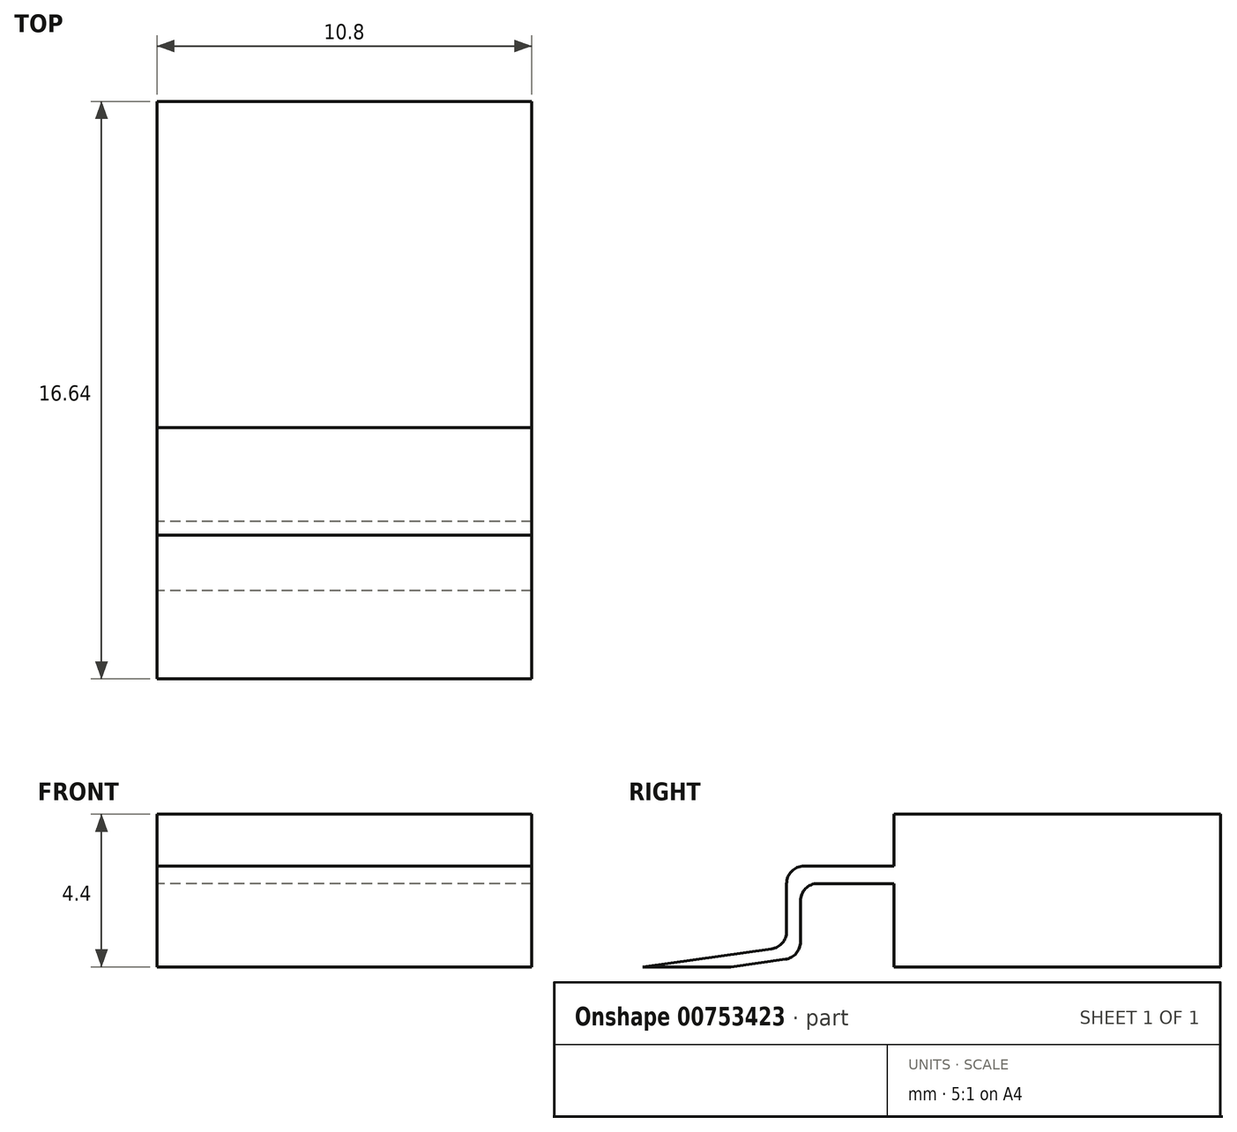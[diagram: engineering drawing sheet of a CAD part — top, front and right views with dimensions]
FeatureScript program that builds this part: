
annotation { "Feature Type Name" : "Feature", "Feature Type Description" : "" }
export const myFeature = defineFeature(function(context is Context, id is Id, definition is map)
    precondition{}
    {
        {
            var Q0;
            Q0=qCreatedBy(makeId("Top.planeOp"),FACE);
            var sketch = newSketch(context, id + "F0", { "sketchPlane" : qUnion([Q0])});
            skLineSegment(sketch, "E0.bottom", {"start": v(-5.4, -4.7) * mm, "end": v(5.4, -4.7) * mm});
            skLineSegment(sketch, "E0.top", {"start": v(-5.4, 4.7) * mm, "end": v(5.4, 4.7) * mm});
            skLineSegment(sketch, "E0.left", {"start": v(-5.4, 4.7) * mm, "end": v(-5.4, -4.7) * mm});
            skLineSegment(sketch, "E0.right", {"start": v(5.4, 4.7) * mm, "end": v(5.4, -4.7) * mm});
            skSolve(sketch);
        }
        {
            var Q0;
            Q0 = qSketchRegion(id + "F0", true);
            extrude(context, id + "F1", {"entities" : qUnion([Q0]), "depth" : 4.4 * mm, "offsetDistance" : 25 * mm});
        }
        {
            var Q0;
            Q0=makeQuery(id+"F1.opExtrude","SWEPT_FACE",FACE,{"disambiguationData":[OSD([sQuery(id+"F0.wireOp",EDGE,"E0.left")])]});
            var sketch = newSketch(context, id + "F2", { "sketchPlane" : qUnion([Q0])});
            skLineSegment(sketch, "E1.bottom", {"start": v(4.7, 2.9) * mm, "end": v(7.8, 2.9) * mm});
            skLineSegment(sketch, "E1.top", {"start": v(4.7, 2.4) * mm, "end": v(7.8, 2.4) * mm});
            skLineSegment(sketch, "E1.left", {"start": v(4.7, 2.9) * mm, "end": v(4.7, 2.4) * mm});
            skLineSegment(sketch, "E1.right", {"start": v(7.8, 2.9) * mm, "end": v(7.8, 2.4) * mm});
            skLineSegment(sketch, "E2.left", {"start": v(7.8, 2.9) * mm, "end": v(7.8, 0.58) * mm});
            skLineSegment(sketch, "E3", {"start": v(7.4, 0.28) * mm, "end": v(9.4, 0) * mm});
            skLineSegment(sketch, "E4", {"start": v(7.4, 0.28) * mm, "end": v(7.8, 0.58) * mm});
            skLineSegment(sketch, "E5", {"start": v(7.8, 0.58) * mm, "end": v(11.94, 0) * mm});
            skLineSegment(sketch, "E6", {"start": v(9.4, 0) * mm, "end": v(9.8, 0.3) * mm});
            skLineSegment(sketch, "E7", {"start": v(7.4, 0.28) * mm, "end": v(7.4, 2.4) * mm});
            skLineSegment(sketch, "E8", {"start": v(9.4, 0) * mm, "end": v(11.94, 0) * mm});
            skSolve(sketch);
        }
        {
            var Q0;
            {var subQ5=sQuery(id+"F2.wireOp",EDGE,"E1.bottom");Q0=makeQuery(id+"F2.imprint","IMPRINT",FACE,{"disambiguationData":[TD([[makeQuery(id+"F2.imprint","IMPRINT",EDGE,{"derivedFrom":subQ5}),-1.0]])]});}
            var Q1;
            {var subQ4=sQuery(id+"F2.wireOp",EDGE,"E4");Q1=makeQuery(id+"F2.imprint","IMPRINT",FACE,{"disambiguationData":[TD([[makeQuery(id+"F2.imprint","IMPRINT",EDGE,{"derivedFrom":subQ4}),1.0]])]});}
            var Q2;
            Q2=makeQuery(id+"F2.imprint","IMPRINT",FACE,{"disambiguationData":[TD([[makeQuery(id+"F2.imprint","IMPRINT",EDGE,{"derivedFrom":sQuery(id+"F2.wireOp",EDGE,"E3")}),1.0]])]});
            var Q3;
            {var subQ2=sQuery(id+"F2.wireOp",EDGE,"E6");Q3=makeQuery(id+"F2.imprint","IMPRINT",FACE,{"disambiguationData":[TD([[makeQuery(id+"F2.imprint","IMPRINT",EDGE,{"derivedFrom":subQ2}),-1.0]])]});}
            var Q4;
            Q4=makeQuery(id+"F1.opExtrude","SWEPT_FACE",FACE,{"disambiguationData":[OSD([sQuery(id+"F0.wireOp",EDGE,"E0.right")])]});
            extrude(context, id + "F3", {"entities" : qUnion([Q0, Q1, Q2, Q3]), "operationType" : NewBodyOperationType.ADD, "endBound" : BoundingType.UP_TO_SURFACE, "oppositeDirection" : true, "depth" : 25 * mm, "endBoundEntityFace" : qUnion([Q4]), "offsetDistance" : 25 * mm});
        }
        {
            var Q0;
            Q0=makeQuery(id+"F3.opExtrude","SWEPT_EDGE",EDGE,{"disambiguationData":[OSD([sQuery(id+"F2.wireOp",EDGE,"E1.bottom"),sQuery(id+"F2.wireOp",EDGE,"E2.left")])]});
            var Q1;
            Q1=makeQuery(id+"F3.opExtrude","SWEPT_EDGE",EDGE,{"disambiguationData":[OSD([sQuery(id+"F2.wireOp",EDGE,"E1.top"),sQuery(id+"F2.wireOp",EDGE,"E7")])]});
            var Q2;
            Q2=makeQuery(id+"F3.opExtrude","SWEPT_EDGE",EDGE,{"disambiguationData":[OSD([sQuery(id+"F2.wireOp",EDGE,"E3"),sQuery(id+"F2.wireOp",EDGE,"E4"),sQuery(id+"F2.wireOp",EDGE,"E7")])]});
            var Q3;
            Q3=makeQuery(id+"F3.opExtrude","SWEPT_EDGE",EDGE,{"disambiguationData":[OSD([sQuery(id+"F2.wireOp",EDGE,"E2.left"),sQuery(id+"F2.wireOp",EDGE,"E4"),sQuery(id+"F2.wireOp",EDGE,"E5")])]});
            fillet(context, id + "F4", {"entities" : qUnion([Q0, Q1, Q2, Q3]), "radius" : 0.5 * mm, "tangentPropagation" : true, "allowEdgeOverflow" : false});
        }
    });
